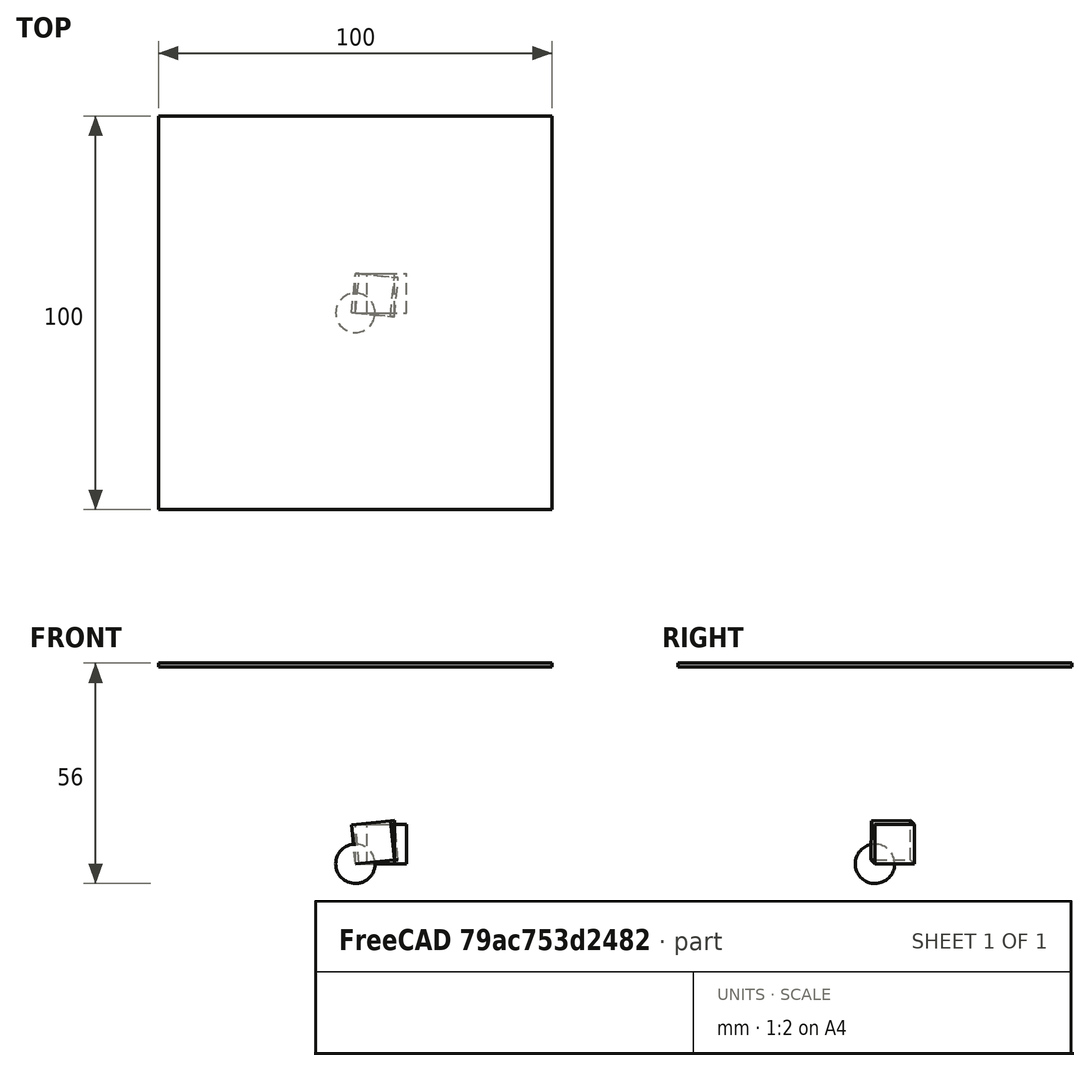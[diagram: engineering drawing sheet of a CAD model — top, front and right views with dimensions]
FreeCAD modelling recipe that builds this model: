
FCSTD DOCUMENT  (FreeCAD 1.1R44874 (Git))
Label: main
License: All rights reserved
LicenseURL: https://en.wikipedia.org/wiki/All_rights_reserved
objects: App::Part×10, App::Point×10, App::Link×9, App::LinkGroupPython×5, Part::Box×4, App::DocumentObjectGroup×2, Part::Sphere×1, Part::FeaturePython×1, Part::Feature×1, App::LinkGroup×1
note: 7 computed .brp shape members not serialized (recipe doc carries the construction recipe); baked Part::Feature solids carry a one-line shape summary decoded from their .brp

FEATURE [App::LinkGroupPython] OpticalPointSource  label="OpticalPointSource001"  # WARN: FeaturePython — macro-defined, semantics opaque (R4)
  Divergence = -
  FanPhi0 = 0
  Fans = 1
  FocalLength = 0
  LinkMode = 0
  MaxIntersectionsScale = 1
  MaxRayLengthScale = 1
  PhiDomain = 0, 2*pi
  PhiResolutionNumericMode = 100
  Placement = pos=(0,0,4) rot=(0,0,1;0rad)
  PowerDensity = 1
  RadiusDomain = 0, 10
  RadiusResolutionNumericMode = 100000
  RandomNumberGeneratorMode = numeric
  RaysPerFan = 50
  RaysPerIterationScale = 1
  RecordRays = true
  ThetaDomain = 0, pi/4
  ThetaResolutionNumericMode = 100000
  Wavelength = 500
FEATURE [App::Part] Part
  Group = -> [OpticalPointSource]
  Origin = -> Origin
  Placement = pos=(5,0,0) rot=(0,0,1;0rad)
FEATURE [App::Point] Origin001
  Role = Origin
FEATURE [App::Point] Origin003
  Role = Origin
FEATURE [Part::Box] Box  label="Cube"
  AttacherType = Attacher::AttachEngine3D
  Height = 10
  Length = 10
  Placement = pos=(3,0,0) rot=(0,0,1;0rad)
  Width = 10
FEATURE [App::Part] Part001
  Group = -> [Box]
  Origin = -> Origin002
  Placement = pos=(-3,4,0) rot=(1,1,0;0.10472rad)
FEATURE [App::LinkGroupPython] OpticalMirrorGroup  label="OpticalMirrorGroup001"  # WARN: FeaturePython — macro-defined, semantics opaque (R4)
  AbsorptionLength = inf
  ElementList = -> [Part001]
  GratingDiffractionOrder = 1
  GratingLinesOrientation = (0,0,1)
  GratingLinesPerMillimeter = 1000
  GratingType = 0
  LinkMode = 0
  ModifyPhiDomain = 0, 2*pi
  ModifyThetaDomain = -pi/2, pi/2
  OpticalType = 0
  Placement = pos=(0,0,-3) rot=(0,0,1;-0.10472rad)
  PowerPhiDomain = 0, 2*pi
  PowerThetaDomain = -pi/2, pi/2
  RecordHits = false
  Reflectivity = 1
  RefractiveIndex = 2
FEATURE [App::Point] Origin005  label="Origin006"
  Role = Origin
FEATURE [App::Part] Part003
  Group = -> [Part]
  Origin = -> Origin006
  Placement = pos=(0,0,-12) rot=(0,0,1;0rad)
FEATURE [App::Point] Origin007  label="Origin009"
  Role = Origin
FEATURE [App::DocumentObjectGroup] Group
  Group = -> [Part003]
FEATURE [App::Part] Part004
  Group = -> [Part003,Group]
  Origin = -> Origin008
  Placement = pos=(0,0,-3) rot=(0,0,1;0rad)
FEATURE [App::Point] Origin009  label="Origin011"
  Role = Origin
FEATURE [Part::Box] Box001  label="Cube001"
  AttacherType = Attacher::AttachEngine3D
  Height = 10
  Length = 10
  Placement = pos=(0,0,0) rot=(0,1,1;-0.139626rad)
  Width = 10
FEATURE [Part::Sphere] Sphere
  Angle1 = -90
  Angle2 = 90
  Angle3 = 360
  AttacherType = Attacher::AttachEngine3D
  Radius = 5
FEATURE [App::LinkGroupPython] OpticalLensGroup  label="OpticalLensGroup003"  # WARN: FeaturePython — macro-defined, semantics opaque (R4)
  AbsorptionLength = inf
  ElementList = -> [Sphere]
  GratingDiffractionOrder = 1
  GratingLinesOrientation = (0,0,1)
  GratingLinesPerMillimeter = 1000
  GratingType = 0
  LinkMode = 0
  ModifyPhiDomain = 0, 2*pi
  ModifyThetaDomain = -pi/2, pi/2
  OpticalType = 1
  Placement = pos=(5,0,10) rot=(0,0,1;0rad)
  PowerPhiDomain = 0, 2*pi
  PowerThetaDomain = -pi/2, pi/2
  RecordHits = false
  Reflectivity = 1
  RefractiveIndex = 2
FEATURE [App::Part] Part005
  Group = -> [OpticalLensGroup]
  Origin = -> Origin010
  Placement = pos=(0,0,9) rot=(8,0,7;0rad)
FEATURE [App::Part] Part002
  Group = -> [OpticalMirrorGroup,Part005]
  Origin = -> Origin004
  Placement = pos=(1,0,5) rot=(4,0,5;-0.122173rad)
FEATURE [App::Point] Origin011  label="Origin014"
  Role = Origin
FEATURE [App::LinkGroupPython] OpticalMirrorGroup001  label="OpticalMirrorGroup002"  # WARN: FeaturePython — macro-defined, semantics opaque (R4)
  AbsorptionLength = inf
  ElementList = -> [Box001]
  GratingDiffractionOrder = 1
  GratingLinesOrientation = (0,0,1)
  GratingLinesPerMillimeter = 1000
  GratingType = 0
  LinkMode = 0
  ModifyPhiDomain = 0, 2*pi
  ModifyThetaDomain = -pi/2, pi/2
  OpticalType = 0
  Placement = pos=(0,-13,3) rot=(1,0,1;-0.15708rad)
  PowerPhiDomain = 0, 2*pi
  PowerThetaDomain = -pi/2, pi/2
  RecordHits = false
  Reflectivity = 1
  RefractiveIndex = 2
FEATURE [Part::FeaturePython] OpticalSimulationSettings  # WARN: FeaturePython — macro-defined, semantics opaque (R4)
  Active = true
  DistanceTolerance = 1e-06
  EnableStoreSingleShotData = false
  EndAfterHits = inf
  EndAfterIterations = inf
  EndAfterRays = inf
  MaxIntersections = 100
  MaxRayLength = 1000
  RaysPerIteration = 100
  SequentialMode = false
  ShowRaysInContinuousMode = true
  StoreHitFanIndex = false
  StoreHitInitDirection = false
  StoreHitInitPhi = false
  StoreHitInitPoint = false
  StoreHitInitPower = false
  StoreHitInitTheta = false
  StoreHitInitWavelength = false
  StoreHitRayIndex = false
  StoreHitTotalFanCount = false
  StoreHitTotalRaysInFan = false
  WorkerProcessCount = 2
FEATURE [Part::Feature] RaySegment
FEATURE [Part::Box] Box002  label="Cube002"
  AttacherType = Attacher::AttachEngine3D
  Height = 1
  Length = 100
  Placement = pos=(-50,-50,50) rot=(0,0,1;0rad)
  Width = 100
FEATURE [App::LinkGroupPython] OpticalAbsorberGroup  # WARN: FeaturePython — macro-defined, semantics opaque (R4)
  AbsorptionLength = inf
  ElementList = -> [Box002]
  GratingDiffractionOrder = 1
  GratingLinesOrientation = (0,0,1)
  GratingLinesPerMillimeter = 1000
  GratingType = 0
  LinkMode = 0
  ModifyPhiDomain = 0, 2*pi
  ModifyThetaDomain = -pi/2, pi/2
  OpticalType = 3
  PowerPhiDomain = 0, 2*pi
  PowerThetaDomain = -pi/2, pi/2
  RecordHits = true
  Reflectivity = 1
  RefractiveIndex = 2
FEATURE [App::Link] Link  label="sourceDirectLink"
  LinkPlacement = pos=(-100,0,0) rot=(0,0,1;0rad)
  LinkedObject = -> OpticalPointSource
  Placement = pos=(-100,0,0) rot=(0,0,1;0rad)
FEATURE [App::Link] Link001  label="sourceIndirectLink"
  LinkPlacement = pos=(100,0,0) rot=(0,0,1;0rad)
  LinkedObject = -> Part003
  Placement = pos=(100,0,0) rot=(0,0,1;0rad)
FEATURE [App::Point] Origin013  label="Origin017"
  Role = Origin
FEATURE [App::Point] Origin015  label="Origin020"
  Role = Origin
FEATURE [App::Point] Origin017  label="Origin022"
  Role = Origin
FEATURE [Part::Box] Box003  label="ShiftedCube"
  AttacherType = Attacher::AttachEngine3D
  Height = 10
  Length = 10
  Width = 10
FEATURE [App::Part] Part008  label="xshift"
  Group = -> [Box003]
  Origin = -> Origin016
  Placement = pos=(3,0,0) rot=(0,0,1;0rad)
FEATURE [App::Part] Part007  label="yshift"
  Group = -> [Part008]
  Origin = -> Origin014
  Placement = pos=(0,3,0) rot=(0,0,1;0rad)
FEATURE [App::Part] Part006  label="zshift"
  Group = -> [Part007]
  Origin = -> Origin012
  Placement = pos=(0,0,3) rot=(0,0,1;0rad)
FEATURE [App::Link] Link002  label="noshiftlink"
  LinkedObject = -> Box003
FEATURE [App::Link] Link003  label="xlink"
  LinkedObject = -> Part008
FEATURE [App::Link] Link005  label="zlink"
  LinkedObject = -> Part006
FEATURE [App::Point] Origin019  label="Origin025"
  Role = Origin
FEATURE [App::Link] Link006  label="ShiftedCube001"
  LinkTransform = true
  LinkedObject = -> Box003
FEATURE [App::Link] Link007  label="zlink001"
  LinkedObject = -> Link005
FEATURE [App::Link] Link008  label="zshift001"
  LinkedObject = -> Part006
FEATURE [App::LinkGroup] LinkGroup
  ElementList = -> [Link006,Link007,Link008]
  LinkMode = 1
  Placement = pos=(0,-30,0) rot=(0,0,1;0rad)
FEATURE [App::Link] Link009  label="ylink"
  LinkedObject = -> Part007
FEATURE [App::DocumentObjectGroup] Group001  label="placementTests"
  Group = -> [Part006,Link002,Link003,Link005,Link009]
FEATURE [App::Part] Part009  label="placementTestsPart"
  Group = -> [Part006,Link002,Link003,Link005,Group001,LinkGroup,Link009]
  Origin = -> Origin018
  Placement = pos=(0,0,-100) rot=(0,0,1;0rad)
